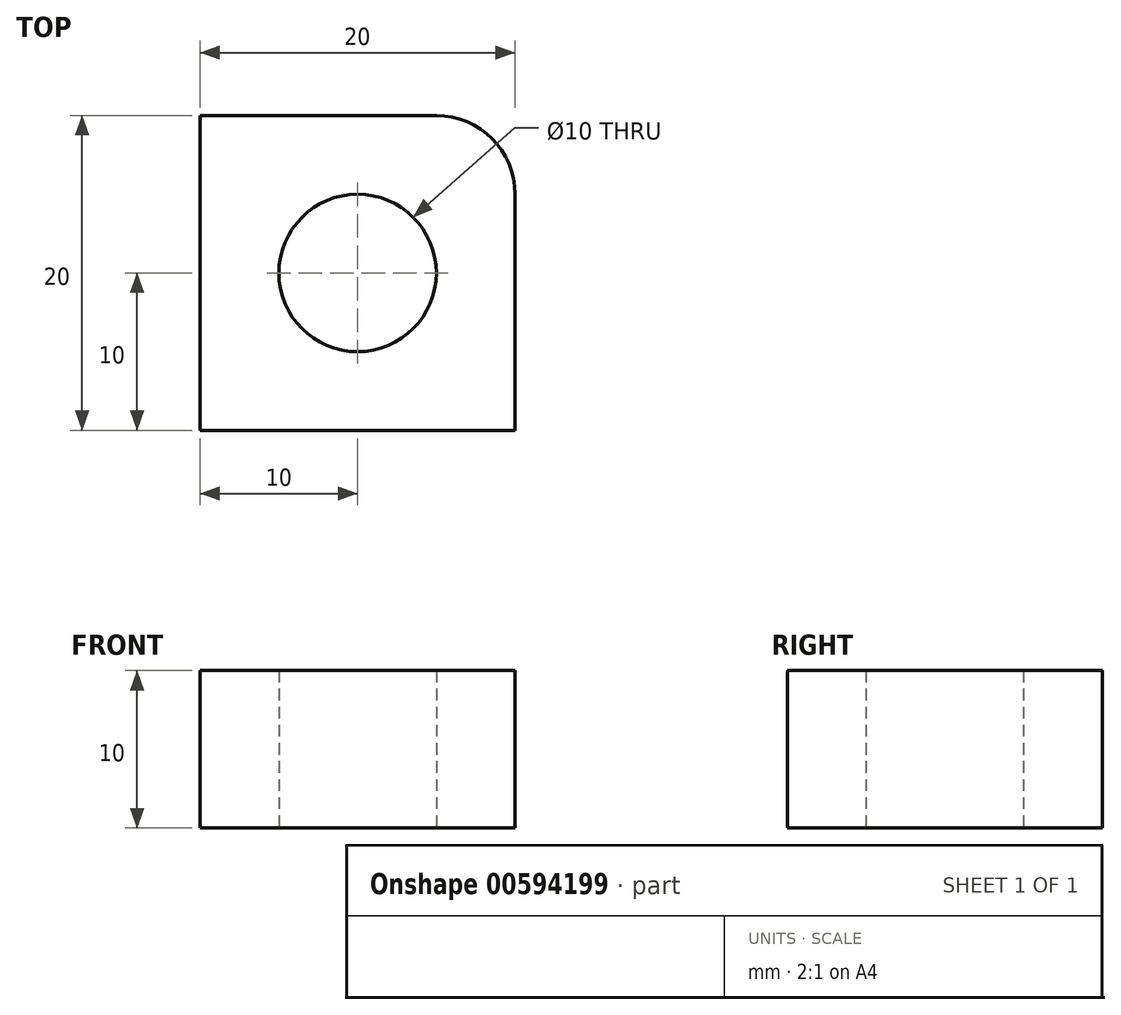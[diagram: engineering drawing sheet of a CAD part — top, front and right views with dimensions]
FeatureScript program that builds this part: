
annotation { "Feature Type Name" : "Feature", "Feature Type Description" : "" }
export const myFeature = defineFeature(function(context is Context, id is Id, definition is map)
    precondition{}
    {
        {
            var Q0;
            Q0=qCreatedBy(makeId("Top.planeOp"),FACE);
            var sketch = newSketch(context, id + "F0", { "sketchPlane" : qUnion([Q0])});
            skLineSegment(sketch, "E0.bottom", {"start": v(5, 10) * mm, "end": v(-10, 10) * mm});
            skLineSegment(sketch, "E0.top", {"start": v(10, -10) * mm, "end": v(-10, -10) * mm});
            skLineSegment(sketch, "E0.left", {"start": v(10, 5) * mm, "end": v(10, -10) * mm});
            skLineSegment(sketch, "E0.right", {"start": v(-10, 10) * mm, "end": v(-10, -10) * mm});
            skPoint(sketch, "E0.middle", {"position": v(0, 0) * mm});
            skCircle(sketch, "E1", {"center": v(0, 0) * mm, "radius": 5 * mm});
            skPoint(sketch, "E2.visualSharp", {"position": v(10, 10) * mm});
            skArc(sketch, "E2.filletArc", {"start": v(10, 5) * mm, "mid": v(8.54, 8.54) * mm, "end": v(5, 10) * mm});
            skSolve(sketch);
        }
        {
            var Q0;
            Q0 = qSketchRegion(id + "F0", true);
            extrude(context, id + "F1", {"entities" : qUnion([Q0]), "depth" : 10 * mm, "offsetDistance" : 25 * mm});
        }
    });
